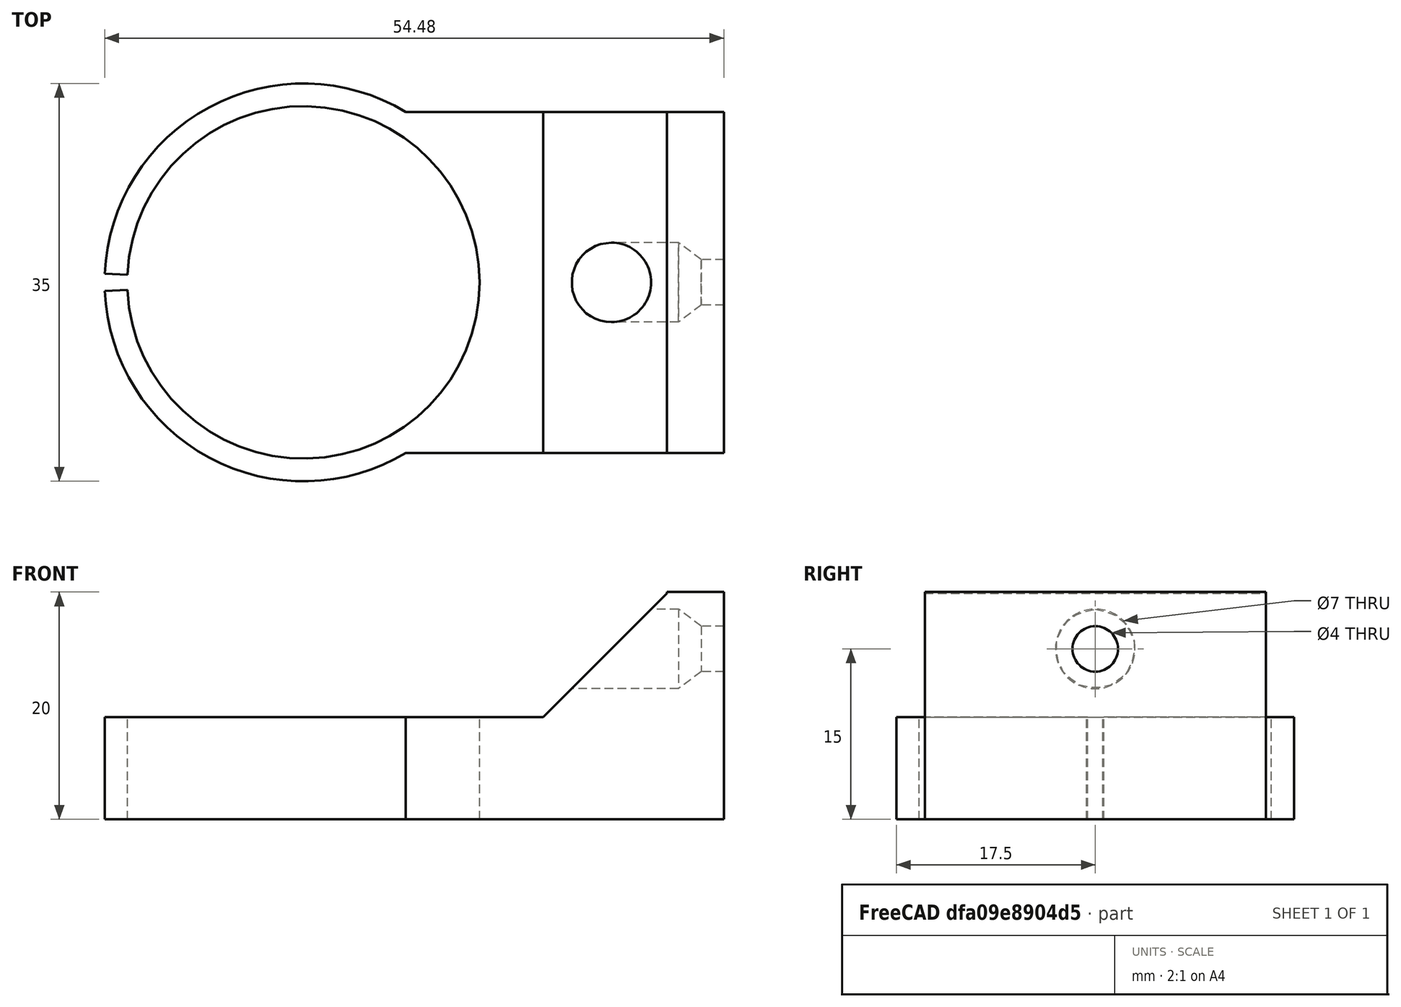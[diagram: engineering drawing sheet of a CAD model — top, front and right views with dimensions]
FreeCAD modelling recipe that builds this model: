
FCSTD DOCUMENT  (FreeCAD 0.16R6703 (Git))
Label: Altavoz
License: All rights reserved
LicenseURL: http://en.wikipedia.org/wiki/All_rights_reserved
objects: Part::Cylinder×4, Part::MultiFuse×4, Part::Box×2, Part::Cone×1, Part::Chamfer×1, Part::Cut×1
note: 13 computed .brp shape members not serialized (recipe doc carries the construction recipe); baked Part::Feature solids carry a one-line shape summary decoded from their .brp

FEATURE [Part::Cylinder] Cylinder
  Angle = 360
  Height = 9
  Radius = 15.5
FEATURE [Part::Cylinder] Cylinder001
  Angle = 355
  Height = 9
  Placement = pos=(0,0,0) rot=(0,0,1;3.18523rad)
  Radius = 17.5
FEATURE [Part::Box] Box  label="Cube"
  Height = 9
  Length = 24
  Placement = pos=(8,-15,0) rot=(0,0,1;0rad)
  Width = 30
FEATURE [Part::Box] Box001  label="Cube001"
  Height = 20
  Length = 5
  Placement = pos=(32,-15,0) rot=(0,0,1;0rad)
  Width = 30
FEATURE [Part::Cylinder] Cylinder002
  Angle = 360
  Height = 10
  Placement = pos=(15,-5,0) rot=(0,0,1;0rad)
  Radius = 2
FEATURE [Part::Cylinder] Cylinder003
  Angle = 360
  Height = 10
  Placement = pos=(15,-5,5) rot=(0,0,1;0rad)
  Radius = 3.5
FEATURE [Part::Cone] Cone
  Angle = 360
  Height = 2
  Placement = pos=(15,-5,3) rot=(0,0,1;0rad)
  Radius1 = 2
  Radius2 = 3.5
FEATURE [Part::MultiFuse] Fusion
  Placement = pos=(38,5,0) rot=(0,-1,0;1.5708rad)
  Shapes = -> [Cylinder002,Cylinder003,Cone]
FEATURE [Part::MultiFuse] Fusion002
  Shapes = -> [Cylinder,Fusion]
FEATURE [Part::MultiFuse] Fusion003
  Shapes = -> [Box,Box001]
FEATURE [Part::Chamfer] Chamfer
  Base = -> Fusion003
  Edges = 1 edges r=10.9: [Edge7]
FEATURE [Part::MultiFuse] Fusion004
  Shapes = -> [Chamfer,Cylinder001]
FEATURE [Part::Cut] Cut
  Base = -> Fusion004
  Tool = -> Fusion002
